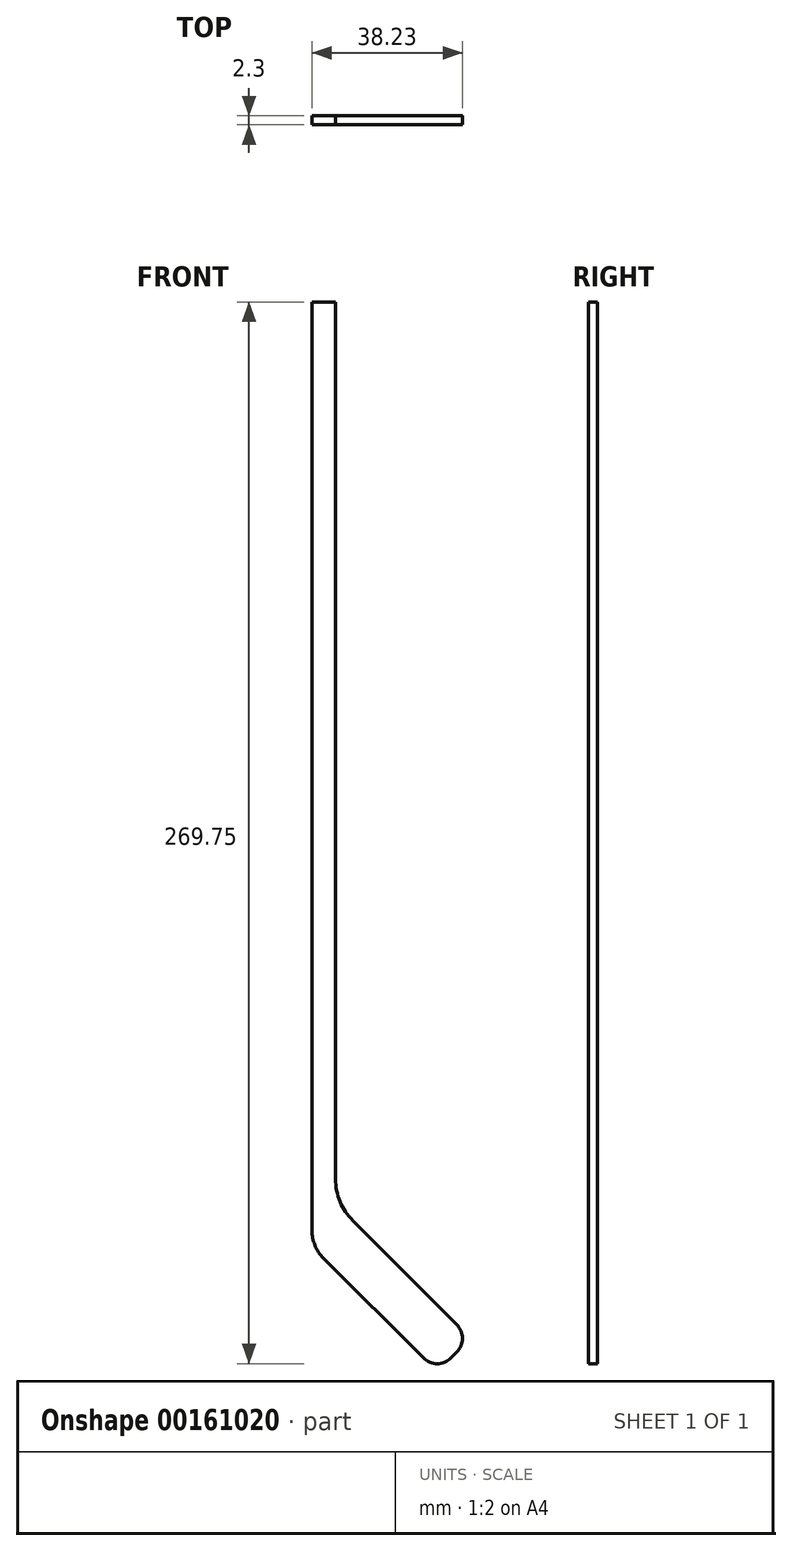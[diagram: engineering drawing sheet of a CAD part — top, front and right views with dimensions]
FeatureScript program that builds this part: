
annotation { "Feature Type Name" : "Feature", "Feature Type Description" : "" }
export const myFeature = defineFeature(function(context is Context, id is Id, definition is map)
    precondition{}
    {
        {
            var Q0;
            Q0=qCreatedBy(makeId("Front.planeOp"),FACE);
            var sketch = newSketch(context, id + "F0", { "sketchPlane" : qUnion([Q0])});
            skLineSegment(sketch, "E0", {"start": v(0, 0) * mm, "end": v(0, 240) * mm});
            skLineSegment(sketch, "E1", {"start": v(0, 240) * mm, "end": v(6, 240) * mm});
            skLineSegment(sketch, "E2", {"start": v(0, 0) * mm, "end": v(31.82, -31.82) * mm});
            skLineSegment(sketch, "E3", {"start": v(31.82, -31.82) * mm, "end": v(40.3, -23.33) * mm});
            skLineSegment(sketch, "E4", {"start": v(6, 10.97) * mm, "end": v(6, 240) * mm});
            skLineSegment(sketch, "E5", {"start": v(6, 10.97) * mm, "end": v(40.3, -23.33) * mm});
            skSolve(sketch);
        }
        {
            var Q0;
            Q0=makeQuery(id+"F0.imprint","IMPRINT",FACE,{"disambiguationData":[TD([[makeQuery(id+"F0.imprint","IMPRINT",EDGE,{"derivedFrom":sQuery(id+"F0.wireOp",EDGE,"E0")}),-1.0]])]});
            extrude(context, id + "F1", {"entities" : qUnion([Q0]), "endBound" : BoundingType.SYMMETRIC, "depth" : 2.3 * mm});
        }
        {
            var Q0;
            Q0=makeQuery(id+"F1.opExtrude","SWEPT_EDGE",EDGE,{"disambiguationData":[OSD([sQuery(id+"F0.wireOp",EDGE,"E2"),sQuery(id+"F0.wireOp",EDGE,"E3")])]});
            var Q1;
            Q1=makeQuery(id+"F1.opExtrude","SWEPT_EDGE",EDGE,{"disambiguationData":[OSD([sQuery(id+"F0.wireOp",EDGE,"E3"),sQuery(id+"F0.wireOp",EDGE,"fwePRi2J-oRte-dWRm-7DaZ-aHYD94WTmia1")])]});
            fillet(context, id + "F2", {"entities" : qUnion([Q0, Q1]), "radius" : 5 * mm, "tangentPropagation" : true, "allowEdgeOverflow" : false});
        }
        {
            var Q0;
            Q0=makeQuery(id+"F1.opExtrude","SWEPT_EDGE",EDGE,{"disambiguationData":[OSD([sQuery(id+"F0.wireOp",EDGE,"E0"),sQuery(id+"F0.wireOp",EDGE,"E2")])]});
            fillet(context, id + "F3", {"entities" : qUnion([Q0]), "radius" : 10 * mm, "tangentPropagation" : true, "allowEdgeOverflow" : false});
        }
        {
            var Q0;
            Q0=makeQuery(id+"F1.opExtrude","SWEPT_FACE",FACE,{"disambiguationData":[OSD([sQuery(id+"F0.wireOp",EDGE,"E2")])]});
            cPlane(context, id + "F4", {"entities" : qUnion([Q0]), "cplaneType" : CPlaneType.OFFSET, "offset" : 0 * mm, "width" : 150 * mm, "height" : 150 * mm});
        }
        {
            var Q0;
            Q0=makeQuery(id+"F1.opExtrude","SWEPT_EDGE",EDGE,{"disambiguationData":[OSD([sQuery(id+"F0.wireOp",EDGE,"E4"),sQuery(id+"F0.wireOp",EDGE,"E5")])]});
            fillet(context, id + "F5", {"entities" : qUnion([Q0]), "radius" : 15 * mm, "tangentPropagation" : true, "allowEdgeOverflow" : false});
        }
    });
